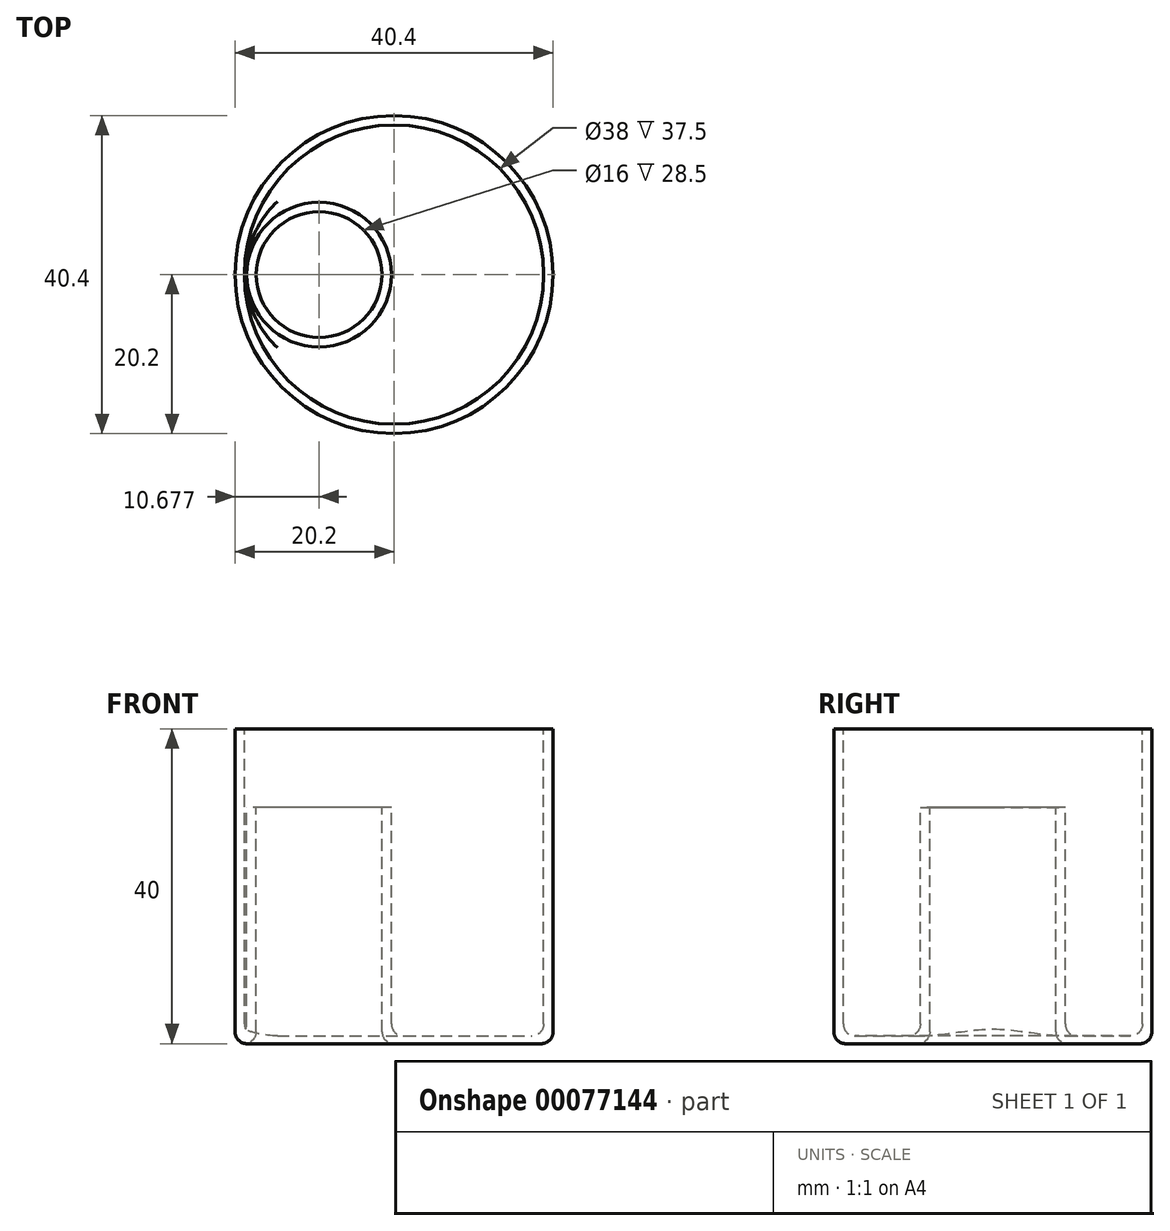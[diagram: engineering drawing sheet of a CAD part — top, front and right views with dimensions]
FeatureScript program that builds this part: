
annotation { "Feature Type Name" : "Feature", "Feature Type Description" : "" }
export const myFeature = defineFeature(function(context is Context, id is Id, definition is map)
    precondition{}
    {
        {
            var Q0;
            Q0=qCreatedBy(makeId("Front.planeOp"),FACE);
            var sketch = newSketch(context, id + "F0", { "sketchPlane" : qUnion([Q0])});
            skLineSegment(sketch, "E0", {"start": v(0, 0) * mm, "end": v(-20.2, 0) * mm});
            skLineSegment(sketch, "E1", {"start": v(-20.2, 0) * mm, "end": v(-20.2, 40) * mm});
            skLineSegment(sketch, "E2", {"start": v(-20.2, 40) * mm, "end": v(-19, 40) * mm});
            skLineSegment(sketch, "E3", {"start": v(-19, 40) * mm, "end": v(-19, 1) * mm});
            skLineSegment(sketch, "E4", {"start": v(-19, 1) * mm, "end": v(0, 1) * mm});
            skLineSegment(sketch, "E5", {"start": v(0, 1) * mm, "end": v(0, 0) * mm});
            skSolve(sketch);
        }
        {
            var Q0;
            Q0=makeQuery(id+"F0.imprint","IMPRINT",FACE,{"disambiguationData":[TD([[makeQuery(id+"F0.imprint","IMPRINT",EDGE,{"derivedFrom":sQuery(id+"F0.wireOp",EDGE,"E0")}),-1.0]])]});
            var Q1;
            Q1=sQuery(id+"F0.wireOp",EDGE,"E5");
            revolve(context, id + "F1", {"entities" : qUnion([Q0]), "axis" : qUnion([Q1]), "revolveType" : RevolveType.FULL});
        }
        {
            var Q0;
            Q0=qCreatedBy(makeId("Front.planeOp"),FACE);
            var sketch = newSketch(context, id + "F2", { "sketchPlane" : qUnion([Q0])});
            skLineSegment(sketch, "E6", {"start": v(-9.52, 25.87) * mm, "end": v(-9.52, -7.77) * mm, "construction": true});
            skLineSegment(sketch, "E7", {"start": v(-18.72, 30) * mm, "end": v(-18.72, 0) * mm});
            skLineSegment(sketch, "E8", {"start": v(-18.72, 0) * mm, "end": v(-17.52, 0) * mm});
            skLineSegment(sketch, "E9", {"start": v(-17.52, 0) * mm, "end": v(-17.52, 30) * mm});
            skLineSegment(sketch, "E10", {"start": v(-17.52, 30) * mm, "end": v(-18.72, 30) * mm});
            skSolve(sketch);
        }
        {
            var Q0;
            Q0=makeQuery(id+"F2.imprint","IMPRINT",FACE,{"disambiguationData":[TD([[makeQuery(id+"F2.imprint","IMPRINT",EDGE,{"derivedFrom":sQuery(id+"F2.wireOp",EDGE,"E7")}),1.0]])]});
            var Q1;
            Q1=sQuery(id+"F2.wireOp",EDGE,"E6");
            revolve(context, id + "F3", {"operationType" : NewBodyOperationType.ADD, "entities" : qUnion([Q0]), "axis" : qUnion([Q1]), "revolveType" : RevolveType.FULL});
        }
        {
            var Q0;
            Q0=makeQuery(id+"F3.boolean.opBoolean","SPLIT",FACE,{"disambiguationData":[TD([makeQuery(id+"F3.opRevolve","SWEPT_FACE",FACE,{"disambiguationData":[OSD([sQuery(id+"F2.wireOp",EDGE,"E9")])]})])],"derivedFrom":makeQuery(id+"F1.opRevolve","SWEPT_FACE",FACE,{"disambiguationData":[OSD([sQuery(id+"F0.wireOp",EDGE,"E4")])]})});
            extrude(context, id + "F4", {"entities" : qUnion([Q0]), "operationType" : NewBodyOperationType.REMOVE, "depth" : 25 * mm, "offsetDistance" : 25 * mm, "symmetric" : true});
        }
        {
            var Q0;
            Q0=makeQuery(id+"F1.opRevolve","SWEPT_EDGE",EDGE,{"disambiguationData":[OSD([sQuery(id+"F0.wireOp",EDGE,"E0"),sQuery(id+"F0.wireOp",EDGE,"E1")])]});
            var Q1;
            Q1=makeQuery(id+"F4.boolean.opBoolean","INTERSECT",EDGE,{"derivedFrom":[makeQuery(id+"F1.opRevolve","SWEPT_FACE",FACE,{"disambiguationData":[OSD([sQuery(id+"F0.wireOp",EDGE,"E0")])]}),makeQuery(id+"F4.opExtrude","SWEPT_FACE",FACE,{"disambiguationData":[OSD([sQuery(id+"F0.wireOp",EDGE,"E4"),sQuery(id+"F2.wireOp",EDGE,"E9")])]})]});
            var Q2;
            Q2=makeQuery(id+"F3.boolean.opBoolean","SPLIT",FACE,{"disambiguationData":[TD([makeQuery(id+"F1.opRevolve","SWEPT_FACE",FACE,{"disambiguationData":[OSD([sQuery(id+"F0.wireOp",EDGE,"E3")])]})])],"derivedFrom":makeQuery(id+"F1.opRevolve","SWEPT_FACE",FACE,{"disambiguationData":[OSD([sQuery(id+"F0.wireOp",EDGE,"E4")])]})});
            fillet(context, id + "F5", {"entities" : qUnion([Q0, Q1, Q2]), "radius" : 1.5 * mm, "tangentPropagation" : true, "allowEdgeOverflow" : false});
        }
    });
